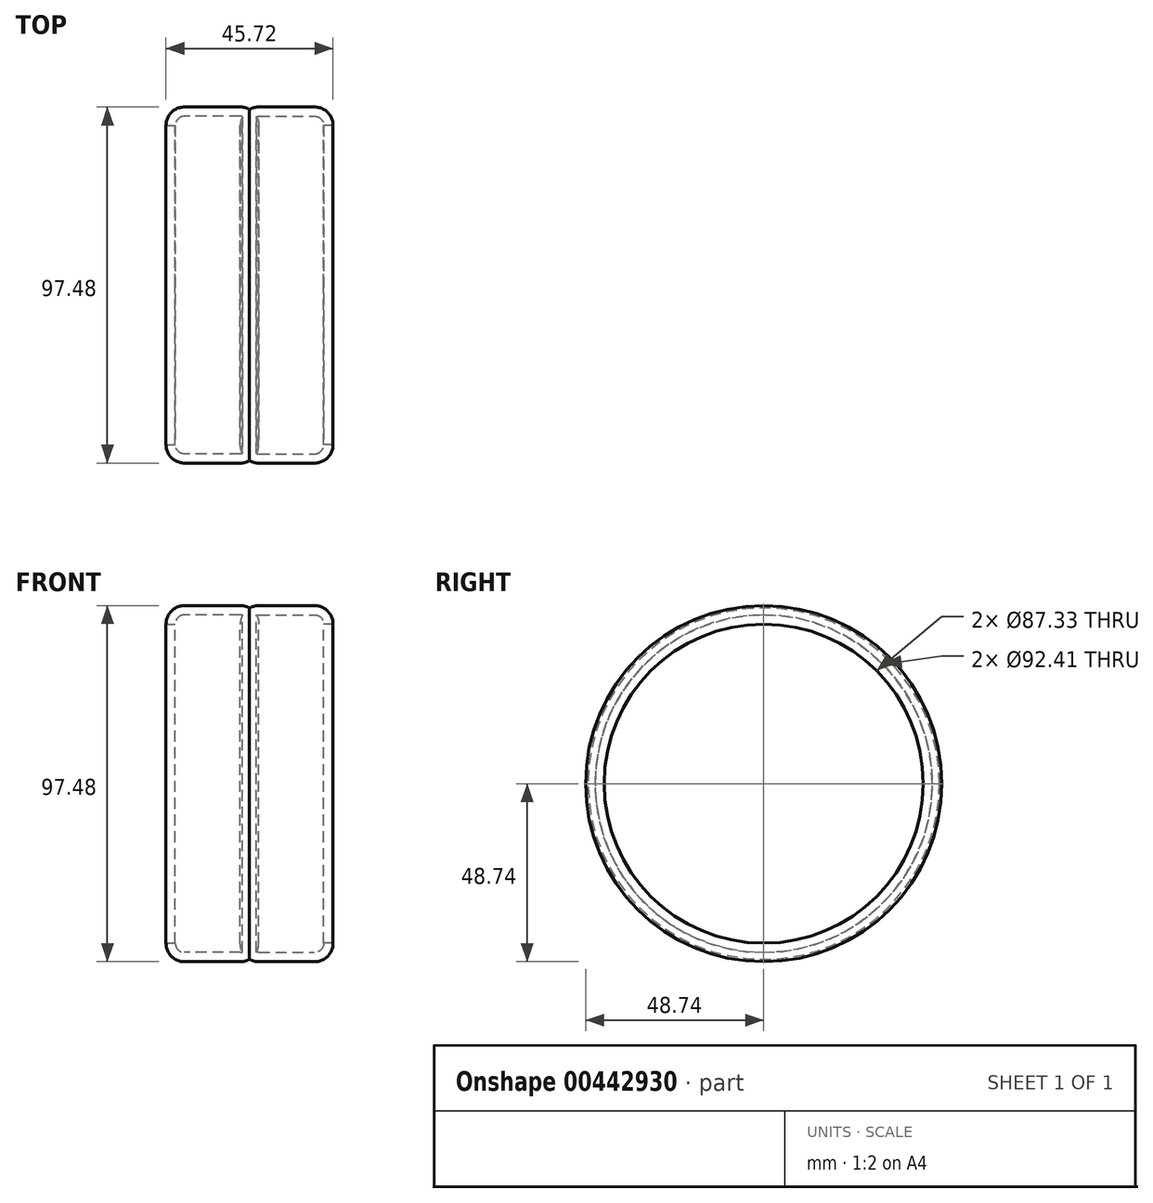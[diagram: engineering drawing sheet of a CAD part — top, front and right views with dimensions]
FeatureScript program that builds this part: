
annotation { "Feature Type Name" : "Feature", "Feature Type Description" : "" }
export const myFeature = defineFeature(function(context is Context, id is Id, definition is map)
    precondition{}
    {
        {
            var Q0;
            Q0=qCreatedBy(makeId("Right.planeOp"),FACE);
            var sketch = newSketch(context, id + "F0", { "sketchPlane" : qUnion([Q0])});
            skCircle(sketch, "E0", {"center": v(0, 0) * mm, "radius": 48.74 * mm});
            skSolve(sketch);
        }
        {
            var Q0;
            Q0=makeQuery(id+"F0.imprint","IMPRINT",FACE,{"disambiguationData":[TD([[makeQuery(id+"F0.imprint","IMPRINT",EDGE,{"derivedFrom":sQuery(id+"F0.wireOp",EDGE,"E0")}),1.0]])]});
            extrude(context, id + "F1", {"entities" : qUnion([Q0]), "depth" : 25.4 * mm});
        }
        {
            var Q0;
            Q0=makeQuery(id+"F1.opExtrude","SWEPT_FACE",FACE,{"disambiguationData":[OSD([sQuery(id+"F0.wireOp",EDGE,"E0")])]});
            var Q1;
            Q1=makeQuery(id+"F1.opExtrude","CAP_FACE",FACE,{"disambiguationData":[OSD([sQuery(id+"F0.wireOp",EDGE,"E0")])],"isStart":false});
            fillet(context, id + "F2", {"entities" : qUnion([Q0, Q1]), "radius" : 5.08 * mm, "tangentPropagation" : true, "allowEdgeOverflow" : false});
        }
        {
            var Q0;
            Q0=makeQuery(id+"F1.opExtrude","CAP_FACE",FACE,{"disambiguationData":[OSD([sQuery(id+"F0.wireOp",EDGE,"E0")])],"isStart":true});
            shell(context, id + "F3", {"entities" : qUnion([Q0]), "thickness" : 2.54 * mm});
        }
        {
            var Q0;
            Q0=makeQuery(id+"F1.opExtrude","SWEPT_BODY",BODY,{"disambiguationData":[OSD([sQuery(id+"F0.wireOp",EDGE,"E0")])]});
            var Q1;
            {var subQ0=sQuery(id+"F0.wireOp",EDGE,"E0");Q1=makeQuery(id+"F3.opShell","OFFSET_FACE",FACE,{"disambiguationData":[OSD([subQ0]),TDD([makeQuery(id+"F1.opExtrude","CAP_FACE",FACE,{"disambiguationData":[OSD([subQ0])],"isStart":false})])]});}
            mirror(context, id + "F4", {"operationType" : NewBodyOperationType.ADD, "entities" : qUnion([Q0]), "mirrorPlane" : qUnion([Q1])});
        }
    });
